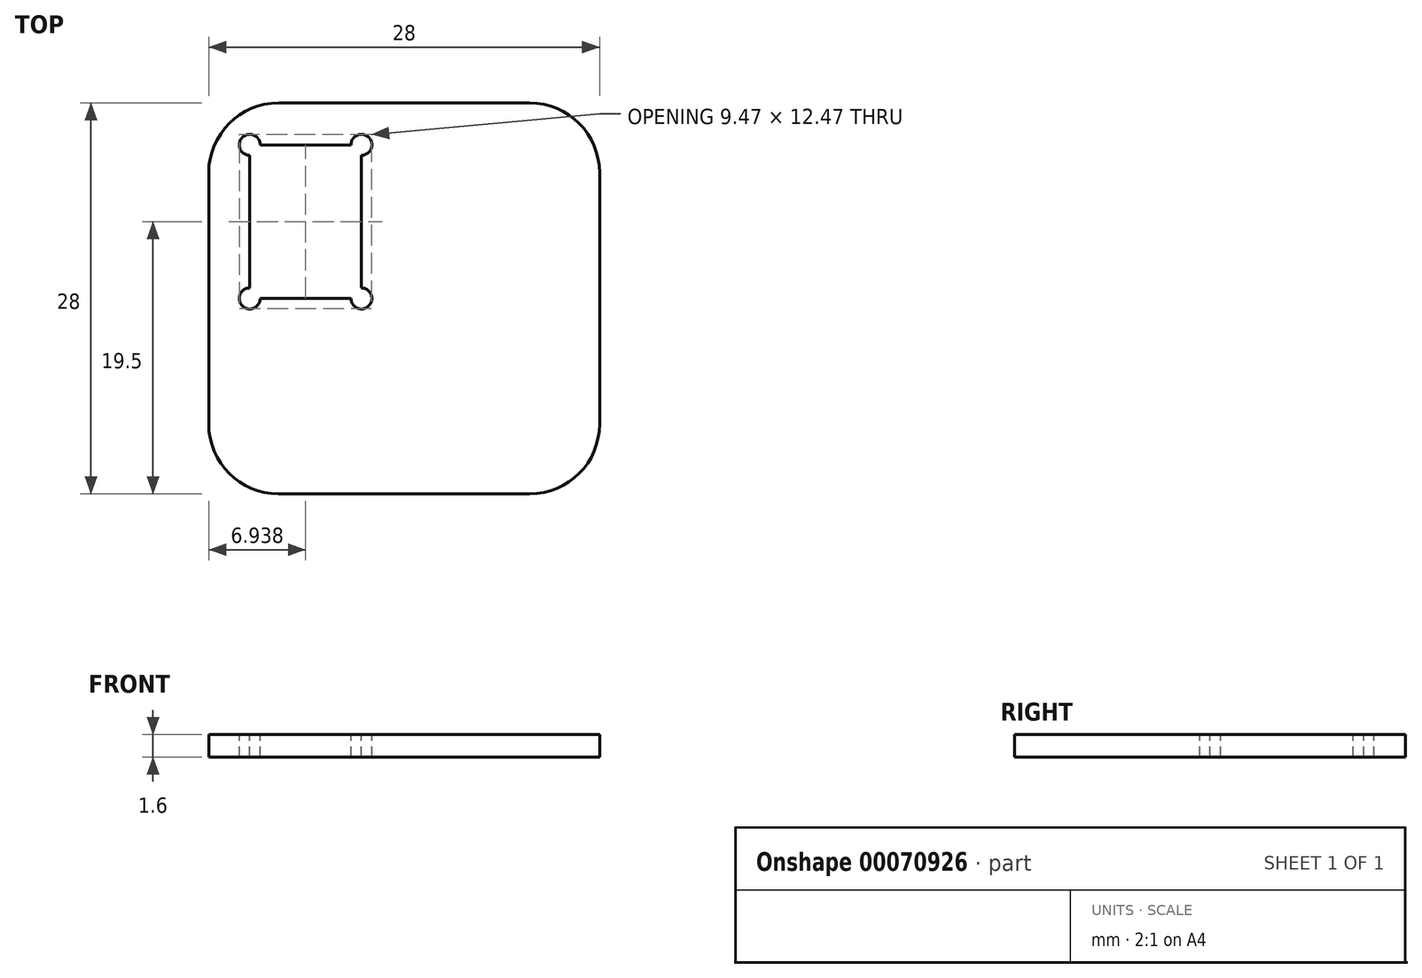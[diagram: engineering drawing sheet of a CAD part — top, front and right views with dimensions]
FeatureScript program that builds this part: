
annotation { "Feature Type Name" : "Feature", "Feature Type Description" : "" }
export const myFeature = defineFeature(function(context is Context, id is Id, definition is map)
    precondition{}
    {
        {
            var Q0;
            Q0=qCreatedBy(makeId("Top.planeOp"),FACE);
            var sketch = newSketch(context, id + "F0", { "sketchPlane" : qUnion([Q0])});
            skLineSegment(sketch, "E0.bottom", {"start": v(-9, 14) * mm, "end": v(9, 14) * mm});
            skLineSegment(sketch, "E0.top", {"start": v(-9, -14) * mm, "end": v(9, -14) * mm});
            skLineSegment(sketch, "E0.left", {"start": v(-14, 9) * mm, "end": v(-14, -9) * mm});
            skLineSegment(sketch, "E0.right", {"start": v(14, 9) * mm, "end": v(14, -9) * mm});
            skPoint(sketch, "E0.middle", {"position": v(0, 0) * mm});
            skPoint(sketch, "E1.visualSharp", {"position": v(-14, 14) * mm});
            skArc(sketch, "E1.filletArc", {"start": v(-9, 14) * mm, "mid": v(-12.54, 12.54) * mm, "end": v(-14, 9) * mm});
            skPoint(sketch, "E2.visualSharp", {"position": v(14, 14) * mm});
            skArc(sketch, "E2.filletArc", {"start": v(14, 9) * mm, "mid": v(12.54, 12.54) * mm, "end": v(9, 14) * mm});
            skPoint(sketch, "E3.visualSharp", {"position": v(14, -14) * mm});
            skArc(sketch, "E3.filletArc", {"start": v(9, -14) * mm, "mid": v(12.54, -12.54) * mm, "end": v(14, -9) * mm});
            skPoint(sketch, "E4.visualSharp", {"position": v(-14, -14) * mm});
            skArc(sketch, "E4.filletArc", {"start": v(-14, -9) * mm, "mid": v(-12.54, -12.54) * mm, "end": v(-9, -14) * mm});
            skSolve(sketch);
        }
        {
            var Q0;
            Q0=makeQuery(id+"F0.imprint","IMPRINT",FACE,{"disambiguationData":[TD([[makeQuery(id+"F0.imprint","IMPRINT",EDGE,{"derivedFrom":sQuery(id+"F0.wireOp",EDGE,"E0.bottom")}),-1.0]])]});
            extrude(context, id + "F1", {"entities" : qUnion([Q0]), "depth" : 1.6 * mm});
        }
        {
            var Q0;
            Q0=makeQuery(id+"F1.opExtrude","CAP_FACE",FACE,{"disambiguationData":[OSD([sQuery(id+"F0.wireOp",EDGE,"E0.bottom"),sQuery(id+"F0.wireOp",EDGE,"E0.top"),sQuery(id+"F0.wireOp",EDGE,"E0.left"),sQuery(id+"F0.wireOp",EDGE,"E0.right"),sQuery(id+"F0.wireOp",EDGE,"E1.filletArc"),sQuery(id+"F0.wireOp",EDGE,"E2.filletArc"),sQuery(id+"F0.wireOp",EDGE,"E3.filletArc"),sQuery(id+"F0.wireOp",EDGE,"E4.filletArc")])],"isStart":false});
            var sketch = newSketch(context, id + "F2", { "sketchPlane" : qUnion([Q0])});
            skLineSegment(sketch, "E5.bottom", {"start": v(-10.31, 11) * mm, "end": v(-3.81, 11) * mm});
            skLineSegment(sketch, "E5.top", {"start": v(-10.31, 0) * mm, "end": v(-3.81, 0) * mm});
            skLineSegment(sketch, "E5.left", {"start": v(-11.06, 10.25) * mm, "end": v(-11.06, 0.75) * mm});
            skLineSegment(sketch, "E5.right", {"start": v(-3.06, 10.25) * mm, "end": v(-3.06, 0.75) * mm});
            skArc(sketch, "E6", {"start": v(-10.31, 11) * mm, "mid": v(-11.6, 11.53) * mm, "end": v(-11.06, 10.25) * mm});
            skArc(sketch, "E7", {"start": v(-3.06, 10.25) * mm, "mid": v(-2.53, 11.53) * mm, "end": v(-3.81, 11) * mm});
            skArc(sketch, "E8", {"start": v(-3.81, 0) * mm, "mid": v(-2.53, -0.53) * mm, "end": v(-3.06, 0.75) * mm});
            skArc(sketch, "E9", {"start": v(-11.06, 0.75) * mm, "mid": v(-11.6, -0.53) * mm, "end": v(-10.31, 0) * mm});
            skSolve(sketch);
        }
        {
            var Q0;
            Q0 = qSketchRegion(id + "F2", true);
            extrude(context, id + "F3", {"entities" : qUnion([Q0]), "operationType" : NewBodyOperationType.REMOVE, "endBound" : BoundingType.THROUGH_ALL, "oppositeDirection" : true, "depth" : 25 * mm});
        }
    });
